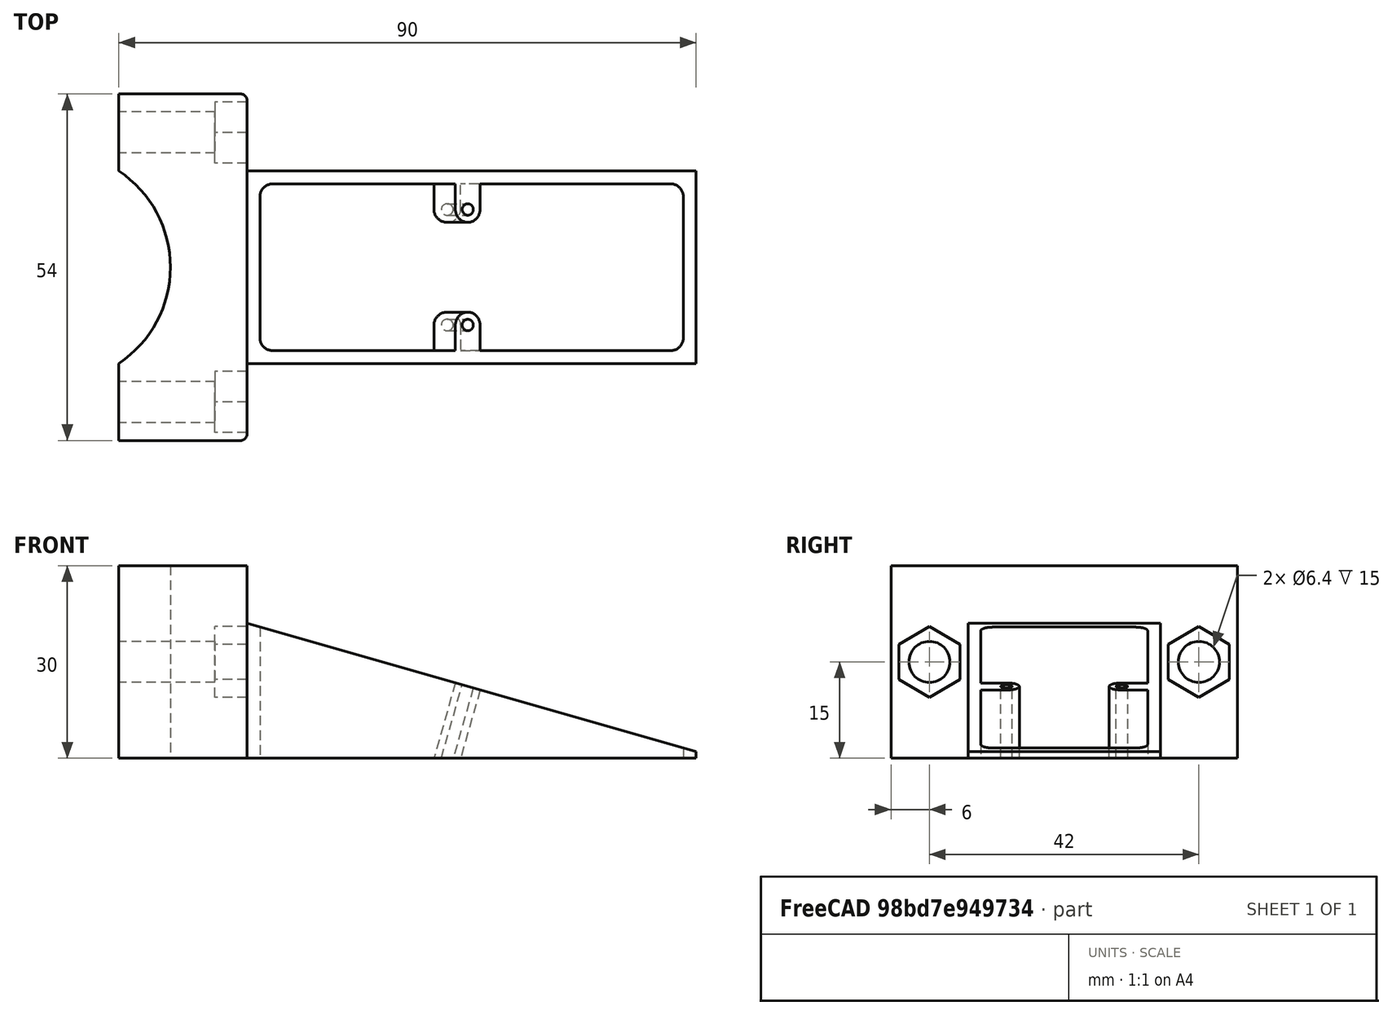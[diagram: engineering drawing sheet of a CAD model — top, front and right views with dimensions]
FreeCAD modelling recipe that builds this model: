
FCSTD DOCUMENT  (FreeCAD 0.18R16117 (Git))
Label: solar_halter_v2
License: All rights reserved
LicenseURL: http://en.wikipedia.org/wiki/All_rights_reserved
objects: TechDraw::DrawViewDimension×12, Part::MultiFuse×5, Sketcher::SketchObject×4, Part::Extrusion×4, Part::Cut×3, TechDraw::DrawProjGroupItem×3, Part::Cylinder×1, Part::Prism×1, Part::FeaturePython×1, Part::Mirroring×1, Part::Box×1, TechDraw::DrawSVGTemplate×1, TechDraw::DrawProjGroup×1, TechDraw::DrawPage×1
note: 21 computed .brp shape members not serialized (recipe doc carries the construction recipe); baked Part::Feature solids carry a one-line shape summary decoded from their .brp

FEATURE [Sketcher::SketchObject] Sketch002  label="Sketch_solar_mastbefestigung1"
  sketch-geometry (8):
    g0: LineSegment StartX=-20 StartY=27 StartZ=0 EndX=-1 EndY=27 EndZ=0
    g1: LineSegment StartX=-2e-16 StartY=26 StartZ=0 EndX=0 EndY=-26 EndZ=0
    g2: LineSegment StartX=-1 StartY=-27 StartZ=0 EndX=-20 EndY=-27 EndZ=0
    g3: LineSegment StartX=-20 StartY=-27 StartZ=0 EndX=-20 EndY=-15 EndZ=0
    g4: LineSegment StartX=-20 StartY=15 StartZ=0 EndX=-20 EndY=27 EndZ=0
    g5: ArcOfCircle CenterX=-29.9499 CenterY=3e-16 CenterZ=0 NormalX=0 NormalY=0 NormalZ=1 AngleXU=0 Radius=18 StartAngle=5.29807 EndAngle=7.2683
    g6: ArcOfCircle CenterX=-1 CenterY=-26 CenterZ=0 NormalX=0 NormalY=0 NormalZ=1 AngleXU=0 Radius=1 StartAngle=4.71239 EndAngle=6.28319
    g7: ArcOfCircle CenterX=-1 CenterY=26 CenterZ=0 NormalX=0 NormalY=0 NormalZ=1 AngleXU=0 Radius=1 StartAngle=0 EndAngle=1.5708
  constraints (21):
    c: Horizontal(g0)
    c: Horizontal(g2)
    c: Coincident(g2,g3)
    c: Vertical(g3)
    c: Coincident(g4,g0)
    c: Vertical(g4)
    c: Coincident(g5,g4)
    c: Coincident(g5,g3)
    c: DistanceY(g3,g3) = 12
    c: Symmetric(g3,g4,g-1)
    c: Tangent(g2,g6) = 1.5708
    c: Tangent(g1,g6) = 1.5708
    c: Tangent(g0,g7) = 1.5708
    c: Tangent(g1,g7) = 1.5708
    c: Radius(g6) = 1
    c: Equal(g6,g7)
    c: DistanceY(g2,g0) = 54
    c: PointOnObject(g1,g-2)
    c: DistanceX(g2,g1) = 20
    c: Symmetric(g2,g0,g-1)
    c: Radius(g5) = 18
FEATURE [Part::Extrusion] Extrude002  label="solar_mastbefestigung1"
  Base = -> Sketch002
  Dir = (0,0,1)
  DirMode = 2
  FaceMakerClass = Part::FaceMakerBullseye
  LengthFwd = 30
  LengthRev = 0
  Solid = true
  Symmetric = false
FEATURE [Part::Cylinder] Cylinder  label="Bohrung"
  Angle = 360
  AttacherType = Attacher::AttachEngine3D
  Height = 30
  Radius = 3.2
FEATURE [Part::Prism] Prism  label="Prisma"
  AttacherType = Attacher::AttachEngine3D
  Circumradius = 5.5
  Height = 5
  Polygon = 6
FEATURE [Part::MultiFuse] Fusion  label="Ausschnitt_M6_Schraube"
  Placement = pos=(0,-21,15) rot=(0,-1,0;1.5708rad)
  Shapes = -> [Cylinder,Prism]
FEATURE [Part::FeaturePython] Clone  label="Ausschnitt_M6_Schraube001"  # Draft clone (typed FeaturePython)
  AttacherType = Attacher::AttachEngine3D
  Fuse = false
  Objects = -> [Fusion]
  Placement = pos=(0,21,15) rot=(0,-1,0;1.5708rad)
  Scale = (1,1,1)
FEATURE [Part::MultiFuse] Fusion001  label="Ausschnitte"
  Shapes = -> [Fusion,Clone]
FEATURE [Sketcher::SketchObject] Sketch003  label="Sketch_Keil2"
  Placement = pos=(0,0,0) rot=(1,0,0;1.5708rad)
  sketch-geometry (4):
    g0: LineSegment StartX=0 StartY=0 StartZ=0 EndX=0 EndY=21 EndZ=0
    g1: LineSegment StartX=0 StartY=21 StartZ=0 EndX=70 EndY=1 EndZ=0
    g2: LineSegment StartX=70 StartY=1 StartZ=0 EndX=70 EndY=0 EndZ=0
    g3: LineSegment StartX=70 StartY=0 StartZ=0 EndX=0 EndY=0 EndZ=0
  constraints (11):
    c: Coincident(g-1,g0)
    c: PointOnObject(g0,g-2)
    c: Coincident(g0,g1)
    c: Coincident(g1,g2)
    c: PointOnObject(g2,g-1)
    c: Coincident(g2,g3)
    c: Coincident(g3,g0)
    c: Vertical(g2)
    c: DistanceY(g2,g2) = 1
    c: DistanceY(g0,g0) = 21
    c: DistanceX(g3,g3) = 70
FEATURE [Part::Extrusion] Extrude003  label="Keil2_roh"
  Base = -> Sketch003
  Dir = (0,-1,0)
  DirMode = 2
  FaceMakerClass = Part::FaceMakerBullseye
  LengthFwd = 30
  LengthRev = 0
  Solid = true
  Symmetric = false
FEATURE [Sketcher::SketchObject] Sketch004  label="Sketch_Keil2_Ausschnitt"
  ExternalGeometry = -> [Extrude003]
  Placement = pos=(0,0,0) rot=(1,0,0;3.14159rad)
  sketch-geometry (8):
    g0: LineSegment StartX=4 StartY=28 StartZ=0 EndX=66 EndY=28 EndZ=0
    g1: LineSegment StartX=68 StartY=26 StartZ=0 EndX=68 EndY=4 EndZ=0
    g2: LineSegment StartX=66 StartY=2 StartZ=0 EndX=4 EndY=2 EndZ=0
    g3: LineSegment StartX=2 StartY=4 StartZ=0 EndX=2 EndY=26 EndZ=0
    g4: ArcOfCircle CenterX=4 CenterY=26 CenterZ=0 NormalX=0 NormalY=0 NormalZ=1 AngleXU=0 Radius=2 StartAngle=1.5708 EndAngle=3.14159
    g5: ArcOfCircle CenterX=4 CenterY=4 CenterZ=0 NormalX=0 NormalY=0 NormalZ=1 AngleXU=0 Radius=2 StartAngle=3.14159 EndAngle=4.71239
    g6: ArcOfCircle CenterX=66 CenterY=4 CenterZ=0 NormalX=0 NormalY=0 NormalZ=1 AngleXU=0 Radius=2 StartAngle=4.71239 EndAngle=6.28319
    g7: ArcOfCircle CenterX=66 CenterY=26 CenterZ=0 NormalX=0 NormalY=0 NormalZ=1 AngleXU=0 Radius=2 StartAngle=0 EndAngle=1.5708
  constraints (20):
    c: Horizontal(g0)
    c: Horizontal(g2)
    c: Vertical(g1)
    c: Vertical(g3)
    c: Tangent(g3,g4) = 1.5708
    c: Tangent(g0,g4) = 1.5708
    c: Tangent(g3,g5) = 1.5708
    c: Tangent(g2,g5) = 1.5708
    c: Tangent(g2,g6) = 1.5708
    c: Tangent(g1,g6) = 1.5708
    c: Tangent(g0,g7) = 1.5708
    c: Tangent(g1,g7) = 1.5708
    c: Radius(g4) = 2
    c: Equal(g4,g5)
    c: Equal(g4,g6)
    c: Equal(g4,g7)
    c: DistanceX(g-1,g3) = 2
    c: DistanceY(g-1,g2) = 2
    c: DistanceY(g0,g-3) = 2
    c: DistanceX(g1,g-3) = 2
FEATURE [Part::Extrusion] Extrude004  label="Keil2_Ausschnitt"
  Base = -> Sketch004
  Dir = (0,0,-1)
  DirMode = 2
  FaceMakerClass = Part::FaceMakerBullseye
  LengthFwd = 30
  LengthRev = 0
  Placement = pos=(0,0,30) rot=(0,0,1;0rad)
  Solid = true
  Symmetric = false
FEATURE [Part::Cut] Cut001  label="Keil2_roh1"
  Base = -> Extrude003
  Tool = -> Extrude004
FEATURE [Sketcher::SketchObject] Sketch  label="Sketch_Schraubbolzen"
  ExternalGeometry = -> [Cut001]
  MapMode = 5
  Placement = pos=(5.54717,0,19.4151) rot=(0,1,0;0.2783rad)
  Support = -> [Cut001]
  sketch-geometry (5):
    g0: LineSegment StartX=32 StartY=-28 StartZ=0 EndX=28 EndY=-28 EndZ=0
    g1: LineSegment StartX=28 StartY=-28 StartZ=0 EndX=28 EndY=-24 EndZ=0
    g2: LineSegment StartX=32 StartY=-28 StartZ=0 EndX=32 EndY=-24 EndZ=0
    g3: ArcOfCircle CenterX=30 CenterY=-24 CenterZ=0 NormalX=0 NormalY=0 NormalZ=1 AngleXU=0 Radius=2 StartAngle=0 EndAngle=3.14159
    g4: Circle CenterX=30 CenterY=-24 CenterZ=0 NormalX=0 NormalY=0 NormalZ=1 AngleXU=0 Radius=0.9
  constraints (15):
    c: PointOnObject(g0,g-4)
    c: Horizontal(g0)
    c: Coincident(g0,g1)
    c: Vertical(g1)
    c: Vertical(g2)
    c: Coincident(g3,g2)
    c: Coincident(g1,g3)
    c: Coincident(g4,g3)
    c: Radius(g4) = 0.9
    c: Radius(g3) = 2
    c: DistanceY(g2,g2) = 4
    c: Horizontal(g3,g2)
    c: Horizontal(g1,g3)
    c: Coincident(g2,g0)
    c: DistanceX(g-1,g3) = 30
FEATURE [Part::Extrusion] Extrude  label="Schraubenbolzen1"
  Base = -> Sketch
  Dir = (0.274721,0,0.961524)
  DirMode = 2
  FaceMakerClass = Part::FaceMakerBullseye
  LengthFwd = 15
  LengthRev = 0
  Reversed = true
  Solid = true
  Symmetric = false
FEATURE [Part::Mirroring] Part__Mirroring  label="Schraubenbolzen2"
  Base = (0,0,0)
  Normal = (0,1,0)
  Placement = pos=(0,-30,0) rot=(0,0,1;0rad)
  Source = -> Extrude
FEATURE [Part::Box] Box  label="Abschneider"
  AttacherType = Attacher::AttachEngine3D
  Height = 10
  Length = 80
  Placement = pos=(0,-35,-10) rot=(0,0,1;0rad)
  Width = 40
FEATURE [Part::MultiFuse] Fusion002  label="Schraubenbolzen"
  Shapes = -> [Part__Mirroring,Extrude]
FEATURE [Part::Cut] Cut
  Base = -> Fusion002
  Tool = -> Box
FEATURE [Part::MultiFuse] Fusion003  label="Keil2"
  Placement = pos=(0,15,0) rot=(0,0,1;0rad)
  Shapes = -> [Cut001,Cut]
FEATURE [Part::MultiFuse] Fusion004  label="solar_halter_roh"
  Shapes = -> [Fusion003,Extrude002]
FEATURE [Part::Cut] Cut002  label="solar_halter"
  Base = -> Fusion004
  Tool = -> Fusion001
FEATURE [TechDraw::DrawSVGTemplate] Template
  EditableTexts = Designed_by_Name=W.Klenner; FC-Date=4.3.2020; FC-SC=1:1; FC-SH=1; FC-Title=Energy Harvester; Subtitle=Solarmodul Halter
  Height = 210
  Orientation = 1
  Width = 297
FEATURE [TechDraw::DrawProjGroupItem] ProjItem  label="Front"
  CoarseView = false
  Direction = (0,0,1)
  Focus = 100
  HardHidden = false
  IsoCount = 0
  IsoHidden = false
  IsoVisible = false
  LockPosition = true
  Perspective = false
  Rotation = 0
  RotationVector = (1,0,0)
  ScaleType = 2
  SeamHidden = false
  SeamVisible = false
  SmoothHidden = false
  SmoothVisible = false
  Source = -> [Cut002]
  Type = 0
  X = 0
  Y = 0
FEATURE [TechDraw::DrawProjGroupItem] ProjItem001  label="Bottom"
  CoarseView = false
  Direction = (0,-1,0)
  Focus = 100
  HardHidden = true
  IsoCount = 0
  IsoHidden = false
  IsoVisible = false
  LockPosition = false
  Perspective = false
  Rotation = 0
  RotationVector = (1,0,0)
  ScaleType = 2
  SeamHidden = false
  SeamVisible = false
  SmoothHidden = true
  SmoothVisible = false
  Source = -> [Cut002]
  Type = 5
  X = 0
  Y = 69
FEATURE [TechDraw::DrawProjGroupItem] ProjItem002  label="Right"
  CoarseView = false
  Direction = (1,0,1e-16)
  Focus = 100
  HardHidden = false
  IsoCount = 0
  IsoHidden = false
  IsoVisible = false
  LockPosition = false
  Perspective = false
  Rotation = 0
  RotationVector = (1e-16,0,-1)
  ScaleType = 2
  SeamHidden = false
  SeamVisible = false
  SmoothHidden = false
  SmoothVisible = false
  Source = -> [Cut002]
  Type = 2
  X = -105
  Y = 0
FEATURE [TechDraw::DrawProjGroup] ProjGroup
  Anchor = -> ProjItem
  AutoDistribute = true
  LockPosition = false
  ProjectionType = 0
  Rotation = 0
  ScaleType = 0
  Source = -> [Cut002]
  Views = -> [ProjItem,ProjItem001,ProjItem002]
  X = 174.033
  Y = 108.387
  spacingX = 15
  spacingY = 15
FEATURE [TechDraw::DrawViewDimension] Dimension
  Arbitrary = false
  FormatSpec = %.2f
  LockPosition = false
  MeasureType = 1
  OverTolerance = 0
  References2D = -> [ProjItem]
  Rotation = 0
  ScaleType = 0
  Type = 1
  UnderTolerance = 0
  X = -34.7247
  Y = -34.8204
FEATURE [TechDraw::DrawViewDimension] Dimension001
  Arbitrary = false
  FormatSpec = %.2f
  LockPosition = false
  MeasureType = 1
  OverTolerance = 0
  References2D = -> [ProjItem]
  Rotation = 0
  ScaleType = 0
  Type = 2
  UnderTolerance = 0
  X = -70.3261
  Y = -1.51406
FEATURE [TechDraw::DrawViewDimension] Dimension002
  Arbitrary = false
  FormatSpec = ⌀%.2f
  LockPosition = false
  MeasureType = 1
  OverTolerance = 0
  References2D = -> [ProjItem]
  Rotation = 0
  ScaleType = 0
  Type = 5
  UnderTolerance = 0
  X = -56.0202
  Y = -8.12086
FEATURE [TechDraw::DrawViewDimension] Dimension003
  Arbitrary = false
  FormatSpec = %.2f
  LockPosition = false
  MeasureType = 1
  OverTolerance = 0
  References2D = -> [ProjItem]
  Rotation = 0
  ScaleType = 0
  Type = 1
  UnderTolerance = 0
  X = 10
  Y = -19.5422
FEATURE [TechDraw::DrawViewDimension] Dimension004
  Arbitrary = false
  FormatSpec = %.2f
  LockPosition = false
  MeasureType = 1
  OverTolerance = 0
  References2D = -> [ProjItem]
  Rotation = 0
  ScaleType = 0
  Type = 2
  UnderTolerance = 0
  X = 14.1857
  Y = 0.38573
FEATURE [TechDraw::DrawViewDimension] Dimension005
  Arbitrary = false
  FormatSpec = %.2f
  LockPosition = false
  MeasureType = 1
  OverTolerance = 0
  References2D = -> [ProjItem]
  Rotation = 0
  ScaleType = 0
  Type = 2
  UnderTolerance = 0
  X = 53.7256
  Y = -0.072714
FEATURE [TechDraw::DrawViewDimension] Dimension006
  Arbitrary = false
  FormatSpec = %.2f
  LockPosition = false
  MeasureType = 1
  OverTolerance = 0
  References2D = -> [ProjItem002]
  Rotation = 0
  ScaleType = 0
  Type = 1
  UnderTolerance = 0
  X = 0.232196
  Y = 43.6749
FEATURE [TechDraw::DrawViewDimension] Dimension007
  Arbitrary = false
  FormatSpec = %.2f
  LockPosition = false
  MeasureType = 1
  OverTolerance = 0
  References2D = -> [ProjItem002]
  Rotation = 0
  ScaleType = 0
  Type = 2
  UnderTolerance = 0
  X = -28.9489
  Y = -0.521092
FEATURE [TechDraw::DrawViewDimension] Dimension008
  Arbitrary = false
  FormatSpec = %.2f
  LockPosition = false
  MeasureType = 1
  OverTolerance = 0
  References2D = -> [ProjItem002]
  Rotation = 0
  ScaleType = 0
  Type = 1
  UnderTolerance = 0
  X = -11.0271
  Y = -37.1538
FEATURE [TechDraw::DrawViewDimension] Dimension009
  Arbitrary = false
  FormatSpec = %.2f
  LockPosition = false
  MeasureType = 1
  OverTolerance = 0
  References2D = -> [ProjItem001]
  Rotation = 0
  ScaleType = 0
  Type = 6
  UnderTolerance = 0
  X = -9.29321
  Y = -7.44252
FEATURE [TechDraw::DrawViewDimension] Dimension010
  Arbitrary = false
  FormatSpec = %.2f
  LockPosition = false
  MeasureType = 1
  OverTolerance = 0
  References2D = -> [ProjItem001]
  Rotation = 0
  ScaleType = 0
  Type = 0
  UnderTolerance = 0
  X = 22.2076
  Y = 0.548864
FEATURE [TechDraw::DrawViewDimension] Dimension011
  Arbitrary = false
  FormatSpec = %.2f
  LockPosition = false
  MeasureType = 1
  OverTolerance = 0
  References2D = -> [ProjItem001]
  Rotation = 0
  ScaleType = 0
  Type = 0
  UnderTolerance = 0
  X = -2.37262
  Y = 10.9741
FEATURE [TechDraw::DrawPage] Page
  KeepUpdated = true
  ProjectionType = 0
  Template = -> Template
  Views = -> [ProjGroup,Dimension,Dimension001,Dimension002,Dimension003,Dimension004,Dimension005,Dimension006,Dimension007,Dimension008,Dimension009,Dimension010,Dimension011]
